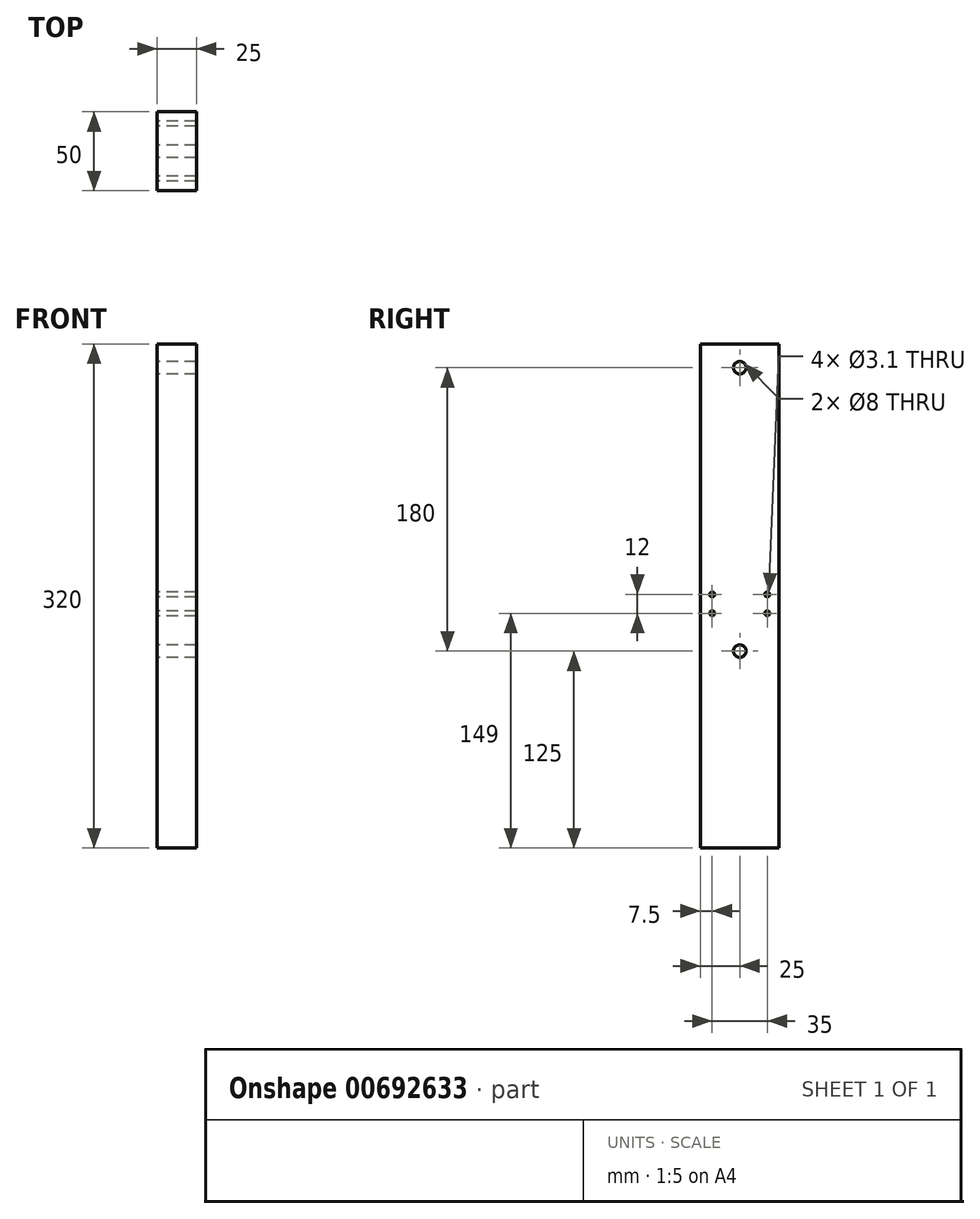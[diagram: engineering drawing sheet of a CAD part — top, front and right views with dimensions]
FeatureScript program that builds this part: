
annotation { "Feature Type Name" : "Feature", "Feature Type Description" : "" }
export const myFeature = defineFeature(function(context is Context, id is Id, definition is map)
    precondition{}
    {
        {
            var Q0;
            Q0=qCreatedBy(makeId("Right.planeOp"),FACE);
            var sketch = newSketch(context, id + "F0", { "sketchPlane" : qUnion([Q0])});
            skLineSegment(sketch, "E0.bottom", {"start": v(0, 0) * mm, "end": v(50, 0) * mm});
            skLineSegment(sketch, "E0.top", {"start": v(0, 320) * mm, "end": v(50, 320) * mm});
            skLineSegment(sketch, "E0.left", {"start": v(0, 0) * mm, "end": v(0, 320) * mm});
            skLineSegment(sketch, "E0.right", {"start": v(50, 0) * mm, "end": v(50, 320) * mm});
            skLineSegment(sketch, "E1", {"start": v(25, 320) * mm, "end": v(25, 0) * mm, "construction": true});
            skCircle(sketch, "E2", {"center": v(25, 305) * mm, "radius": 4 * mm});
            skCircle(sketch, "E3", {"center": v(25, 125) * mm, "radius": 4 * mm});
            skLineSegment(sketch, "E4.bottom", {"start": v(7.5, 161) * mm, "end": v(42.5, 161) * mm, "construction": true});
            skLineSegment(sketch, "E4.top", {"start": v(7.5, 149) * mm, "end": v(42.5, 149) * mm, "construction": true});
            skLineSegment(sketch, "E4.left", {"start": v(7.5, 161) * mm, "end": v(7.5, 149) * mm, "construction": true});
            skLineSegment(sketch, "E4.right", {"start": v(42.5, 161) * mm, "end": v(42.5, 149) * mm, "construction": true});
            skCircle(sketch, "E5", {"center": v(7.5, 161) * mm, "radius": 1.55 * mm});
            skCircle(sketch, "E6", {"center": v(42.5, 161) * mm, "radius": 1.55 * mm});
            skCircle(sketch, "E7", {"center": v(7.5, 149) * mm, "radius": 1.55 * mm});
            skCircle(sketch, "E8", {"center": v(42.5, 149) * mm, "radius": 1.55 * mm});
            skSolve(sketch);
        }
        {
            var Q0;
            Q0 = qSketchRegion(id + "F0", true);
            extrude(context, id + "F1", {"entities" : qUnion([Q0]), "depth" : 25 * mm, "offsetDistance" : 25 * mm});
        }
    });
